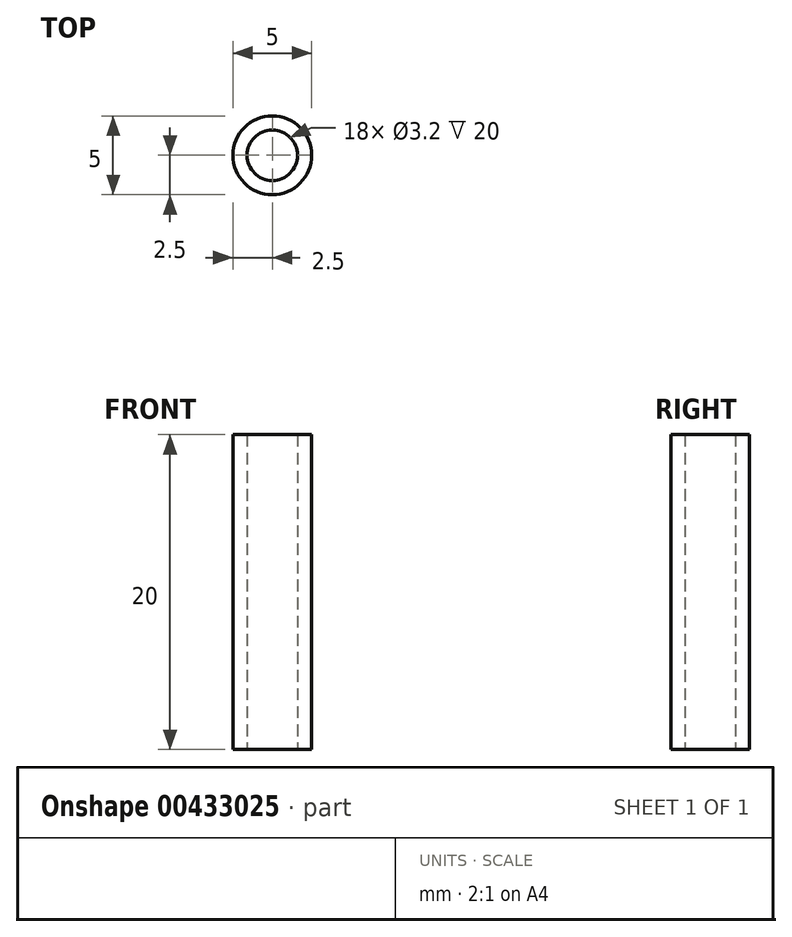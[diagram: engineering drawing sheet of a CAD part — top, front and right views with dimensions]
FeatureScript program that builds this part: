
annotation { "Feature Type Name" : "Feature", "Feature Type Description" : "" }
export const myFeature = defineFeature(function(context is Context, id is Id, definition is map)
    precondition{}
    {
        {
            var Q0;
            Q0=qCreatedBy(makeId("Top.planeOp"),FACE);
            var sketch = newSketch(context, id + "F0", { "sketchPlane" : qUnion([Q0]), "disableImprinting" : false});
            skCircle(sketch, "E0", {"center": v(0, 0) * mm, "radius": 1.6 * mm});
            skCircle(sketch, "E1", {"center": v(0, 0) * mm, "radius": 2.5 * mm});
            skSolve(sketch);
        }
        {
            var Q0;
            Q0=makeQuery(id+"F0.imprint","IMPRINT",FACE,{"disambiguationData":[TD([[makeQuery(id+"F0.imprint","IMPRINT",EDGE,{"derivedFrom":sQuery(id+"F0.wireOp",EDGE,"E0")}),-1.0]])]});
            extrude(context, id + "F1", {"entities" : qUnion([Q0]), "depth" : 20 * mm});
        }
    });
